# Revit family: Haworth_ActiveComponents_Screen_PersonalDividerDrawer
name_source: partatom
category: Furniture Systems
revit_build: Autodesk Revit 2018 (Build: 20170223_1515(x64)
units: mm (PartAtom-declared; Revit-internal decimal feet)

## family parameters
Always vertical = Yes
Cut with Voids When Loaded = No
OmniClass Number = 23.40.70.14.64.21
OmniClass Title = Systems Furniture
Part Type = Normal
Room Calculation Point = No
Round Connector Dimension = Use Diameter
Shared = No
Work Plane-Based = No

## types (1)
- 12h 19d 9w
    Actual Depth = 17"
    Actual Height = 20"
    Actual Width = 9 5/16"
    Assembly Code = E2020200
    Description = Haworth Active Components Screen Personal Divider
    Drawer Height = 3"
    Manufacturer = Haworth
    Model = AUF1-1319
    Mounted Height = 27 3/4"
    Panel Thickness = 1/16"
    Revision Number = 1
    Shelf Height = 1/2"
    Size = Verify Final Dim. w/ Haworth
    Sustainability Info = https://www.haworth.com
    Top Height = 2"
    URL = https://www.haworth.com
    URL - Product = http://www.haworth.com
    Warranty = http://www.haworth.com

## geometry (parser evidence)
native form markers: Sweep x5
no freeform markers — native parametric forms only
